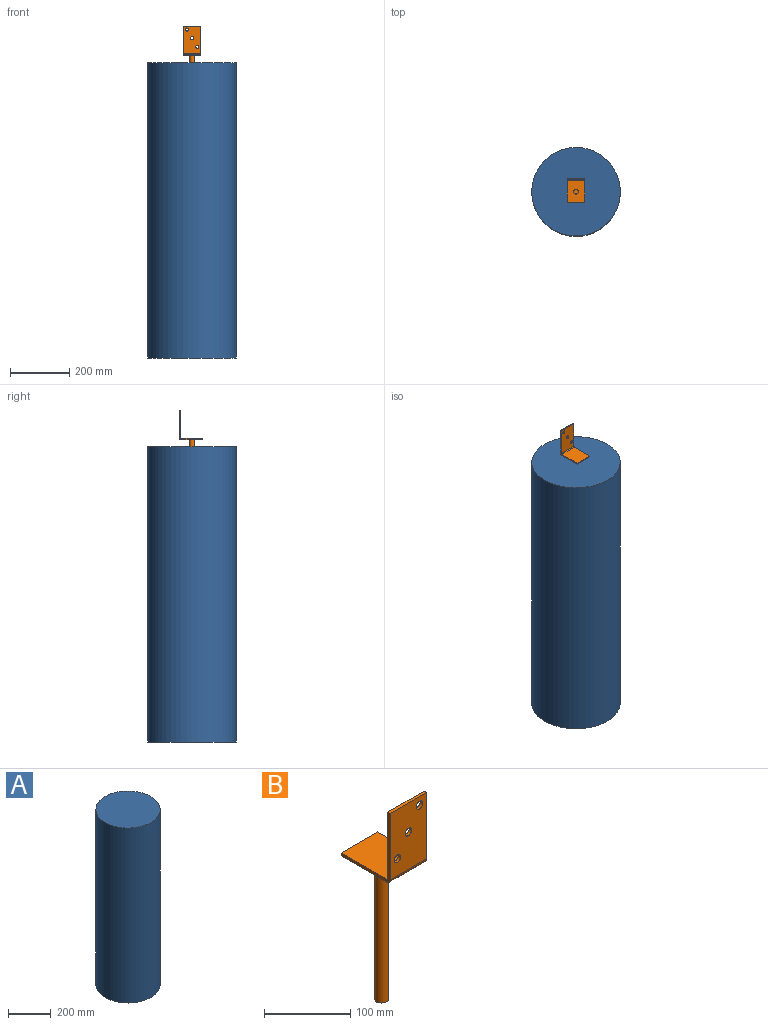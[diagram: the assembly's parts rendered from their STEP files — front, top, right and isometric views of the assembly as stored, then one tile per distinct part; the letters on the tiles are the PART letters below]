
ASSEMBLY  parts=2 mates=2
PART A: 3 faces, bbox 300x300x1000 mm
  f0: cylinder r=150mm len=1000mm, axis (0,0,1), area 942477.8mm2, adj f1,f2
  f1: plane 300x300mm, normal (0,0,-1), area 70685.8mm2, adj f0
  f2: plane 300x300mm, normal (0,0,1), area 70685.8mm2, adj f0
PART B: 15 faces, bbox 60x80x300 mm
  f0: plane 74x60mm, normal (0,0,1), area 4440mm2, adj f5,f6,f7,f10
  f1: plane 94x60mm, normal (0,1,0), area 5380.2mm2, adj f2,f6,f7,f10,f12,f13,f14
  f2: plane 60x4mm, normal (0,0,1), area 240mm2, adj f1,f3,f6,f7
  f3: plane 94x60mm, normal (0,-1,0), area 5380.2mm2, adj f2,f6,f7,f11,f12,f13,f14
  f4: plane 74x60mm, normal (0,0,-1), area 4238.9mm2, adj f5,f6,f7,f8,f11
  f5: plane 60x4mm, normal (0,1,0), area 240mm2, adj f0,f4,f6,f7
  f6: plane 100x80mm, normal (1,0,0), area 697.1mm2, adj f0,f1,f2,f3,f4,f5,f10,f11
  f7: plane 100x80mm, normal (-1,0,0), area 697.1mm2, adj f0,f1,f2,f3,f4,f5,f10,f11
  f8: cylinder r=8mm len=200mm, axis (0,0,1), area 10053.1mm2, adj f4,f9
  f9: plane 16x16mm, normal (0,0,-1), area 201.1mm2, adj f8
  f10: cylinder r=2mm len=60mm, axis (-1,0,0), area 188.5mm2, adj f0,f1,f6,f7
  f11: cylinder r=6mm len=60mm, axis (-1,0,0), area 565.5mm2, adj f3,f4,f6,f7
  f12: cylinder r=5.25mm len=10.5mm, axis (0,-1,0), area 131.9mm2, adj f1,f3
  f13: cylinder r=5.25mm len=10.5mm, axis (0,-1,0), area 131.9mm2, adj f1,f3
  f14: cylinder r=5.25mm len=10.5mm, axis (0,-1,0), area 131.9mm2, adj f1,f3
PLACE A rot(axis=(0,1,0),180deg) t=(0,0,-1000)mm fixed
PLACE B rot(axis=(0,0,1),180deg) t=(0,0,79)mm
MATE cylindrical B.f8 <-> A.f0  axis (0,0,1) through (0,0,-75)mm
MATE planar B.f8 <-> A.f0  axis (0,0,-1) through (0,0,25)mm
